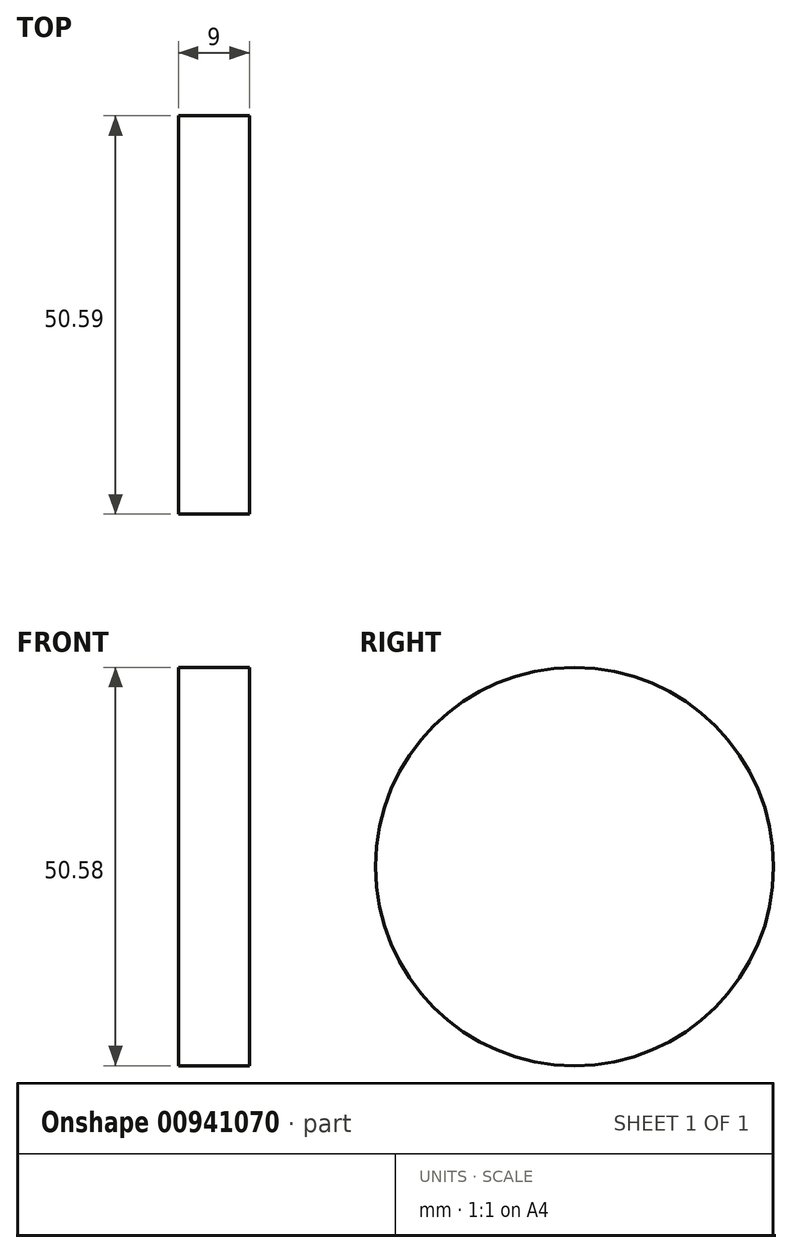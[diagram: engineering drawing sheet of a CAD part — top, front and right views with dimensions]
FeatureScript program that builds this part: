
annotation { "Feature Type Name" : "Feature", "Feature Type Description" : "" }
export const myFeature = defineFeature(function(context is Context, id is Id, definition is map)
    precondition{}
    {
        {
            var Q0;
            Q0=qCreatedBy(makeId("Right.planeOp"),FACE);
            var sketch = newSketch(context, id + "F0", { "sketchPlane" : qUnion([Q0])});
            skCircle(sketch, "E0", {"center": v(-40.66, 43.3) * mm, "radius": 25.3 * mm});
            skSolve(sketch);
        }
        {
            var Q0;
            Q0=makeQuery(id+"F0.imprint","IMPRINT",FACE,{"disambiguationData":[TD([[makeQuery(id+"F0.imprint","IMPRINT",EDGE,{"derivedFrom":sQuery(id+"F0.wireOp",EDGE,"E0")}),1.0]])]});
            extrude(context, id + "F1", {"entities" : qUnion([Q0]), "depth" : 9 * mm, "offsetDistance" : 25 * mm});
        }
    });
